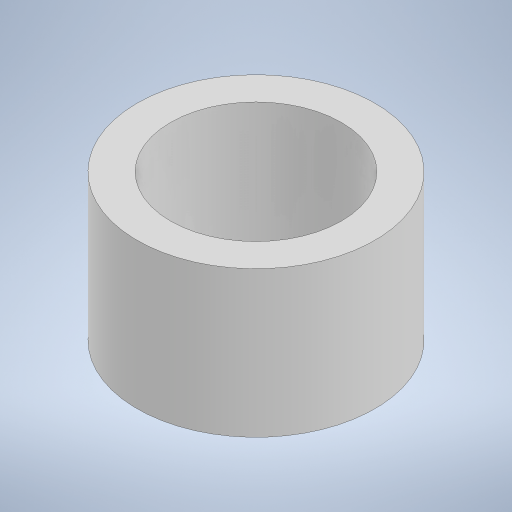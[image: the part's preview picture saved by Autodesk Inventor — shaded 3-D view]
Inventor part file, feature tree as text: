
AUTODESK INVENTOR PART (.ipt)
format: ipt  version: 2024 (Build 280153000, 153)  size: 194,560 bytes
history: native  units: mm
features: other x1, extrude x1
ambient origin geometry x8: Origin, YZ Plane, XZ Plane, XY Plane, X Axis, Y Axis, Z Axis, Center Point
bodies: Body1 (feature_tree)
feature tree (2):
  other  "솔리드1"
  extrude  "돌출1"  Depth=4.1mm
